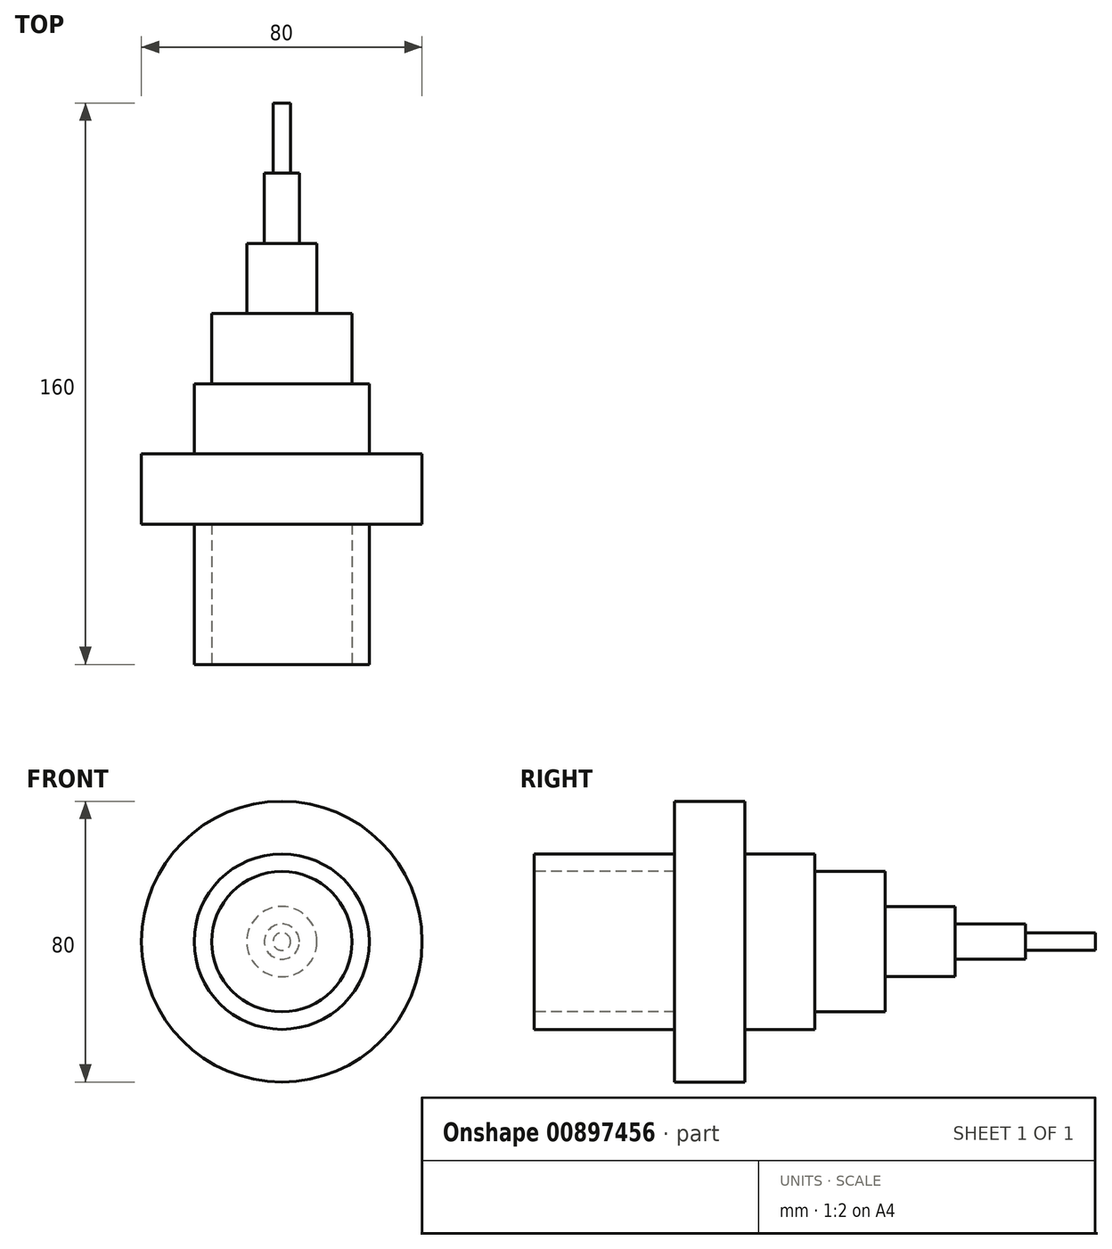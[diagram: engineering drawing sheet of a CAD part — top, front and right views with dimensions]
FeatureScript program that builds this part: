
annotation { "Feature Type Name" : "Feature", "Feature Type Description" : "" }
export const myFeature = defineFeature(function(context is Context, id is Id, definition is map)
    precondition{}
    {
        {
            var Q0;
            Q0=qCreatedBy(makeId("Front.planeOp"),FACE);
            var sketch = newSketch(context, id + "F0", { "sketchPlane" : qUnion([Q0])});
            skCircle(sketch, "E0", {"center": v(0, 0) * mm, "radius": 40 * mm});
            skSolve(sketch);
        }
        {
            var Q0;
            Q0=makeQuery(id+"F0.imprint","IMPRINT",FACE,{"disambiguationData":[TD([[makeQuery(id+"F0.imprint","IMPRINT",EDGE,{"derivedFrom":sQuery(id+"F0.wireOp",EDGE,"E0")}),1.0]])]});
            extrude(context, id + "F1", {"entities" : qUnion([Q0]), "depth" : 20 * mm, "offsetDistance" : 25.4 * mm});
        }
        {
            var Q0;
            Q0=makeQuery(id+"F1.opExtrude","CAP_FACE",FACE,{"disambiguationData":[OSD([sQuery(id+"F0.wireOp",EDGE,"E0")])],"isStart":false});
            var sketch = newSketch(context, id + "F2", { "sketchPlane" : qUnion([Q0])});
            skCircle(sketch, "E1", {"center": v(0, 0) * mm, "radius": 25 * mm});
            skSolve(sketch);
        }
        {
            var Q0;
            Q0=makeQuery(id+"F2.imprint","IMPRINT",FACE,{"disambiguationData":[TD([[makeQuery(id+"F2.imprint","IMPRINT",EDGE,{"derivedFrom":sQuery(id+"F2.wireOp",EDGE,"E1")}),1.0]])]});
            extrude(context, id + "F3", {"entities" : qUnion([Q0]), "operationType" : NewBodyOperationType.ADD, "depth" : 40 * mm, "offsetDistance" : 25.4 * mm});
        }
        {
            var Q0;
            Q0=makeQuery(id+"F3.opExtrude","CAP_FACE",FACE,{"disambiguationData":[OSD([sQuery(id+"F2.wireOp",EDGE,"E1")])],"isStart":false});
            var sketch = newSketch(context, id + "F4", { "sketchPlane" : qUnion([Q0])});
            skCircle(sketch, "E2", {"center": v(0, 0) * mm, "radius": 20 * mm});
            skSolve(sketch);
        }
        {
            var Q0;
            Q0 = qSketchRegion(id + "F4", true);
            var Q1;
            Q1=makeQuery(id+"F4.imprint","IMPRINT",FACE,{"disambiguationData":[TD([[makeQuery(id+"F4.imprint","IMPRINT",EDGE,{"derivedFrom":sQuery(id+"F4.wireOp",EDGE,"E2")}),1.0]])]});
            extrude(context, id + "F5", {"entities" : qUnion([Q0, Q1]), "operationType" : NewBodyOperationType.REMOVE, "oppositeDirection" : true, "depth" : 40 * mm, "offsetDistance" : 25.4 * mm});
        }
        {
            var Q0;
            Q0=makeQuery(id+"F1.opExtrude","CAP_FACE",FACE,{"disambiguationData":[OSD([sQuery(id+"F0.wireOp",EDGE,"E0")])],"isStart":true});
            var sketch = newSketch(context, id + "F6", { "sketchPlane" : qUnion([Q0])});
            skCircle(sketch, "E3", {"center": v(0, 0) * mm, "radius": 25 * mm});
            skSolve(sketch);
        }
        {
            var Q0;
            Q0 = qSketchRegion(id + "F6", true);
            extrude(context, id + "F7", {"entities" : qUnion([Q0]), "operationType" : NewBodyOperationType.ADD, "depth" : 20 * mm, "offsetDistance" : 25.4 * mm});
        }
        {
            var Q0;
            Q0=makeQuery(id+"F7.opExtrude","CAP_FACE",FACE,{"disambiguationData":[OSD([sQuery(id+"F6.wireOp",EDGE,"E3")])],"isStart":false});
            var sketch = newSketch(context, id + "F8", { "sketchPlane" : qUnion([Q0])});
            skCircle(sketch, "E4", {"center": v(0, 0) * mm, "radius": 20 * mm});
            skSolve(sketch);
        }
        {
            var Q0;
            Q0 = qSketchRegion(id + "F8", true);
            extrude(context, id + "F9", {"entities" : qUnion([Q0]), "operationType" : NewBodyOperationType.ADD, "depth" : 20 * mm, "offsetDistance" : 25.4 * mm});
        }
        {
            var Q0;
            Q0=makeQuery(id+"F9.opExtrude","CAP_FACE",FACE,{"disambiguationData":[OSD([sQuery(id+"F8.wireOp",EDGE,"E4")])],"isStart":false});
            var sketch = newSketch(context, id + "F10", { "sketchPlane" : qUnion([Q0])});
            skCircle(sketch, "E5", {"center": v(0, 0) * mm, "radius": 15 * mm});
            skSolve(sketch);
        }
        {
            var Q0;
            Q0=makeQuery(id+"F10.imprint","IMPRINT",FACE,{"disambiguationData":[TD([[makeQuery(id+"F10.imprint","IMPRINT",EDGE,{"derivedFrom":sQuery(id+"F10.wireOp",EDGE,"E5")}),1.0]])]});
            var sketch = newSketch(context, id + "F11", { "sketchPlane" : qUnion([Q0])});
            skCircle(sketch, "E6", {"center": v(0, 0) * mm, "radius": 10 * mm});
            skSolve(sketch);
        }
        {
            var Q0;
            Q0 = qSketchRegion(id + "F11", true);
            extrude(context, id + "F12", {"entities" : qUnion([Q0]), "operationType" : NewBodyOperationType.ADD, "depth" : 20 * mm, "offsetDistance" : 25.4 * mm});
        }
        {
            var Q0;
            Q0=makeQuery(id+"F12.opExtrude","CAP_FACE",FACE,{"disambiguationData":[OSD([sQuery(id+"F11.wireOp",EDGE,"E6")])],"isStart":false});
            var sketch = newSketch(context, id + "F13", { "sketchPlane" : qUnion([Q0])});
            skCircle(sketch, "E7", {"center": v(0, 0) * mm, "radius": 5 * mm});
            skSolve(sketch);
        }
        {
            var Q0;
            Q0 = qSketchRegion(id + "F13", true);
            extrude(context, id + "F14", {"entities" : qUnion([Q0]), "operationType" : NewBodyOperationType.ADD, "depth" : 20 * mm, "offsetDistance" : 25.4 * mm});
        }
        {
            var Q0;
            Q0=makeQuery(id+"F14.opExtrude","CAP_FACE",FACE,{"disambiguationData":[OSD([sQuery(id+"F13.wireOp",EDGE,"E7")])],"isStart":false});
            var sketch = newSketch(context, id + "F15", { "sketchPlane" : qUnion([Q0])});
            skCircle(sketch, "E8", {"center": v(0, 0) * mm, "radius": 2.5 * mm});
            skSolve(sketch);
        }
        {
            var Q0;
            Q0 = qSketchRegion(id + "F15", true);
            extrude(context, id + "F16", {"entities" : qUnion([Q0]), "operationType" : NewBodyOperationType.ADD, "depth" : 20 * mm, "offsetDistance" : 25.4 * mm});
        }
    });
